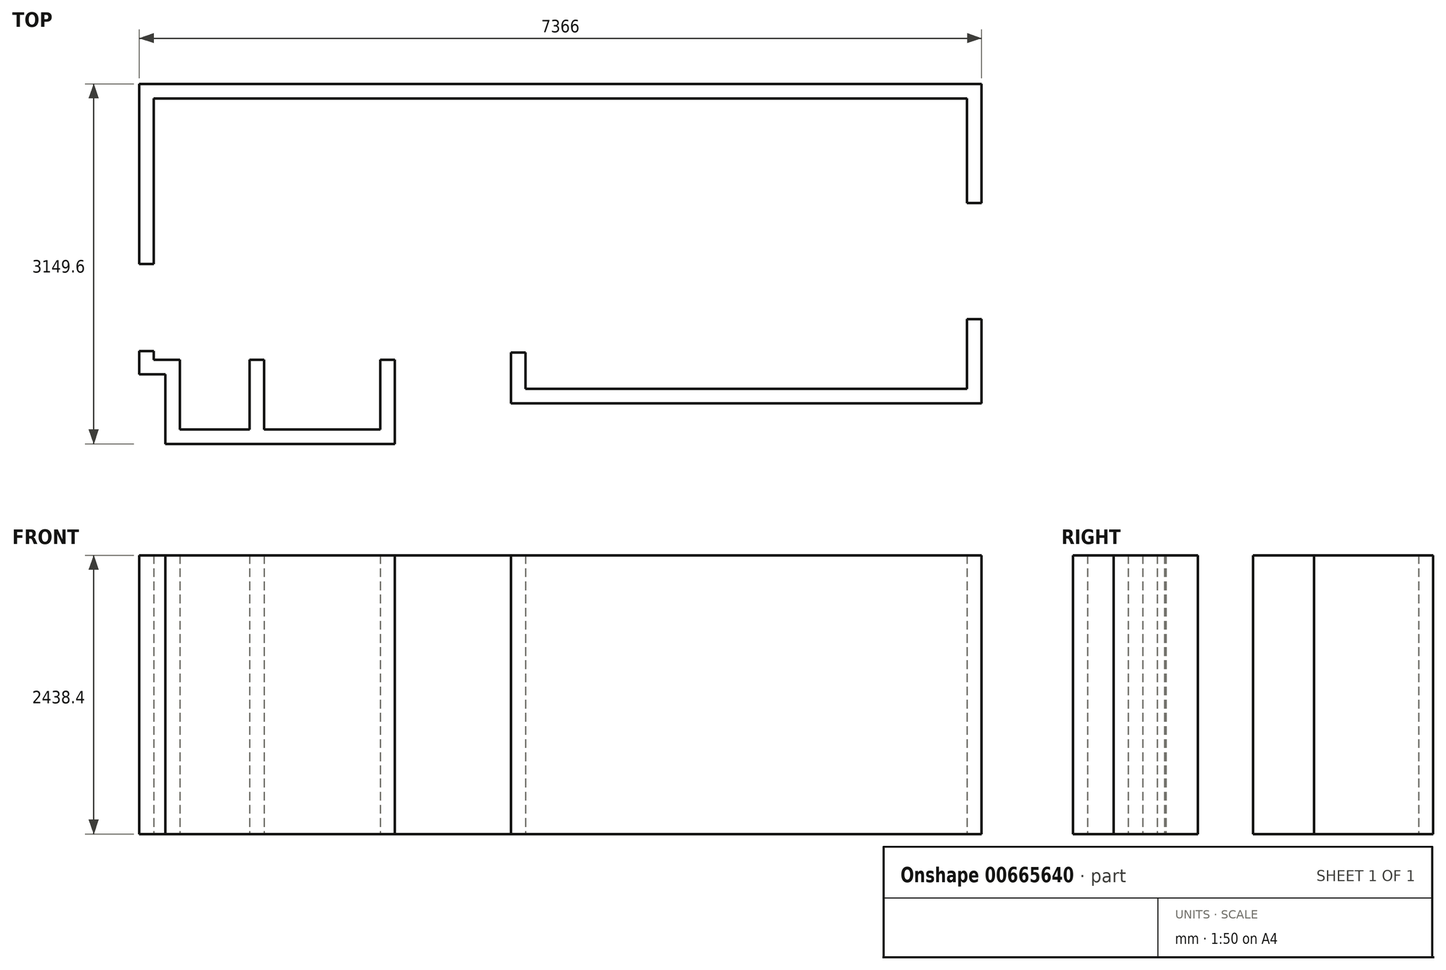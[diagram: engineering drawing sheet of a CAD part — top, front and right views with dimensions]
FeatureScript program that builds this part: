
annotation { "Feature Type Name" : "Feature", "Feature Type Description" : "" }
export const myFeature = defineFeature(function(context is Context, id is Id, definition is map)
    precondition{}
    {
        {
            var Q0;
            Q0=qCreatedBy(makeId("Top.planeOp"),FACE);
            var sketch = newSketch(context, id + "F0", { "sketchPlane" : qUnion([Q0])});
            skLineSegment(sketch, "E0", {"start": v(0, 0) * mm, "end": v(0, -76.2) * mm});
            skLineSegment(sketch, "E1", {"start": v(0, -76.2) * mm, "end": v(228.6, -76.2) * mm});
            skLineSegment(sketch, "E2", {"start": v(228.6, -76.2) * mm, "end": v(228.6, -685.8) * mm});
            skLineSegment(sketch, "E3", {"start": v(228.6, -685.8) * mm, "end": v(838.2, -685.8) * mm});
            skLineSegment(sketch, "E4", {"start": v(838.2, -685.8) * mm, "end": v(838.2, -76.2) * mm});
            skLineSegment(sketch, "E5", {"start": v(838.2, -76.2) * mm, "end": v(965.2, -76.2) * mm});
            skLineSegment(sketch, "E6", {"start": v(965.2, -76.2) * mm, "end": v(965.2, -685.8) * mm});
            skLineSegment(sketch, "E7", {"start": v(965.2, -685.8) * mm, "end": v(1981.2, -685.8) * mm});
            skLineSegment(sketch, "E8", {"start": v(1981.2, -685.8) * mm, "end": v(1981.2, -76.2) * mm});
            skLineSegment(sketch, "E9", {"start": v(1981.2, -76.2) * mm, "end": v(2108.2, -76.2) * mm});
            skLineSegment(sketch, "E10", {"start": v(2108.2, -76.2) * mm, "end": v(2108.2, -812.8) * mm});
            skLineSegment(sketch, "E11", {"start": v(2108.2, -812.8) * mm, "end": v(101.6, -812.8) * mm});
            skLineSegment(sketch, "E12", {"start": v(101.6, -812.8) * mm, "end": v(101.6, -203.2) * mm});
            skLineSegment(sketch, "E13", {"start": v(101.6, -203.2) * mm, "end": v(-127, -203.2) * mm});
            skLineSegment(sketch, "E14", {"start": v(-127, -203.2) * mm, "end": v(-127, 0) * mm});
            skLineSegment(sketch, "E15", {"start": v(-127, 0) * mm, "end": v(0, 0) * mm});
            skLineSegment(sketch, "E16", {"start": v(0, 762) * mm, "end": v(0, 2209.8) * mm});
            skLineSegment(sketch, "E17", {"start": v(0, 2209.8) * mm, "end": v(7112, 2209.8) * mm});
            skLineSegment(sketch, "E18", {"start": v(7112, 2209.8) * mm, "end": v(7112, 1295.4) * mm});
            skLineSegment(sketch, "E19", {"start": v(7112, 1295.4) * mm, "end": v(7239, 1295.4) * mm});
            skLineSegment(sketch, "E20", {"start": v(7239, 1295.4) * mm, "end": v(7239, 2336.8) * mm});
            skLineSegment(sketch, "E21", {"start": v(7239, 2336.8) * mm, "end": v(-127, 2336.8) * mm});
            skLineSegment(sketch, "E22", {"start": v(-127, 2336.8) * mm, "end": v(-127, 762) * mm});
            skLineSegment(sketch, "E23", {"start": v(-127, 762) * mm, "end": v(0, 762) * mm});
            skLineSegment(sketch, "E24", {"start": v(7239, 279.4) * mm, "end": v(7112, 279.4) * mm});
            skLineSegment(sketch, "E25", {"start": v(7112, 279.4) * mm, "end": v(7112, -330.2) * mm});
            skLineSegment(sketch, "E26", {"start": v(7112, -330.2) * mm, "end": v(3251.2, -330.2) * mm});
            skLineSegment(sketch, "E27", {"start": v(3251.2, -330.2) * mm, "end": v(3251.2, -15.39) * mm});
            skLineSegment(sketch, "E28", {"start": v(3251.2, -15.39) * mm, "end": v(3124.2, -15.39) * mm});
            skLineSegment(sketch, "E29", {"start": v(3124.2, -15.39) * mm, "end": v(3124.2, -457.2) * mm});
            skLineSegment(sketch, "E30", {"start": v(3124.2, -457.2) * mm, "end": v(7239, -457.2) * mm});
            skLineSegment(sketch, "E31", {"start": v(7239, -457.2) * mm, "end": v(7239, 279.4) * mm});
            skLineSegment(sketch, "E32", {"start": v(5183.63, 2336.8) * mm, "end": v(5183.63, 2209.8) * mm, "construction": true});
            skLineSegment(sketch, "E33", {"start": v(7112, 1752.6) * mm, "end": v(7239, 1752.6) * mm, "construction": true});
            skLineSegment(sketch, "E34", {"start": v(46.66, -76.2) * mm, "end": v(46.66, -203.2) * mm, "construction": true});
            skLineSegment(sketch, "E35", {"start": v(7006.72, -330.2) * mm, "end": v(7006.72, -457.2) * mm, "construction": true});
            skLineSegment(sketch, "E36", {"start": v(3124.2, -236.3) * mm, "end": v(3251.2, -236.3) * mm, "construction": true});
            skLineSegment(sketch, "E37", {"start": v(101.6, -508) * mm, "end": v(228.6, -508) * mm, "construction": true});
            skSolve(sketch);
        }
        {
            var Q0;
            Q0=makeQuery(id+"F0.imprint","IMPRINT",FACE,{"disambiguationData":[TD([[makeQuery(id+"F0.imprint","IMPRINT",EDGE,{"derivedFrom":sQuery(id+"F0.wireOp",EDGE,"E16")}),1.0]])]});
            var Q1;
            {var subQ1=sQuery(id+"F0.wireOp",EDGE,"E3");Q1=makeQuery(id+"F0.imprint","IMPRINT",FACE,{"disambiguationData":[TD([[makeQuery(id+"F0.imprint","IMPRINT",EDGE,{"derivedFrom":subQ1}),-1.0]])]});}
            var Q2;
            Q2=makeQuery(id+"F0.imprint","IMPRINT",FACE,{"disambiguationData":[TD([[makeQuery(id+"F0.imprint","IMPRINT",EDGE,{"derivedFrom":sQuery(id+"F0.wireOp",EDGE,"E0")}),-1.0]])]});
            var Q3;
            {var subQ1=sQuery(id+"F0.wireOp",EDGE,"E27");Q3=makeQuery(id+"F0.imprint","IMPRINT",FACE,{"disambiguationData":[TD([[makeQuery(id+"F0.imprint","IMPRINT",EDGE,{"derivedFrom":subQ1}),1.0]])]});}
            var Q4;
            Q4=makeQuery(id+"F0.imprint","IMPRINT",FACE,{"disambiguationData":[TD([[makeQuery(id+"F0.imprint","IMPRINT",EDGE,{"derivedFrom":sQuery(id+"F0.wireOp",EDGE,"E24")}),1.0]])]});
            extrude(context, id + "F1", {"entities" : qUnion([Q0, Q1, Q2, Q3, Q4]), "depth" : 2438.4 * mm, "offsetDistance" : 25.4 * mm});
        }
    });
